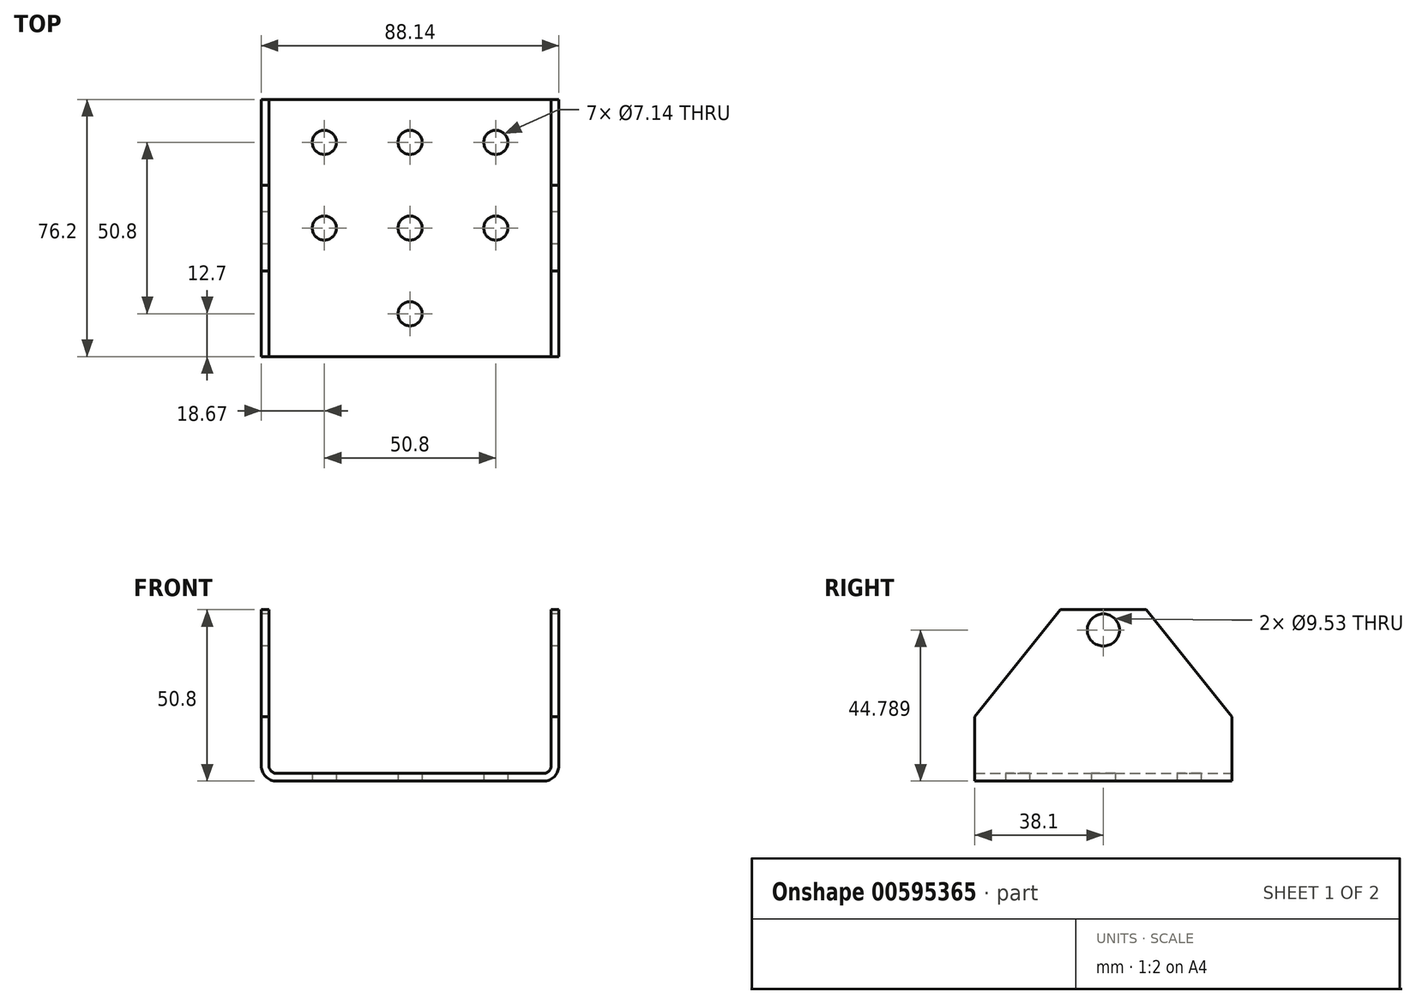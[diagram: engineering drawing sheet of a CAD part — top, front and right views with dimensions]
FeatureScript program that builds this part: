
annotation { "Feature Type Name" : "Feature", "Feature Type Description" : "" }
export const myFeature = defineFeature(function(context is Context, id is Id, definition is map)
    precondition{}
    {
        {
            var Q0;
            Q0=qCreatedBy(makeId("Front.planeOp"),FACE);
            var sketch = newSketch(context, id + "F0", { "sketchPlane" : qUnion([Q0])});
            skLineSegment(sketch, "E0", {"start": v(44.07, 50.8) * mm, "end": v(44.07, 4.57) * mm});
            skLineSegment(sketch, "E1", {"start": v(39.5, 0) * mm, "end": v(-39.5, 0) * mm});
            skLineSegment(sketch, "E2", {"start": v(-44.07, 4.57) * mm, "end": v(-44.07, 50.8) * mm});
            skLineSegment(sketch, "E3.0", {"start": v(-41.78, 4.57) * mm, "end": v(-41.78, 50.8) * mm});
            skLineSegment(sketch, "E3.1", {"start": v(39.5, 2.29) * mm, "end": v(-39.5, 2.29) * mm});
            skLineSegment(sketch, "E3.2", {"start": v(41.78, 50.8) * mm, "end": v(41.78, 4.57) * mm});
            skLineSegment(sketch, "E4", {"start": v(41.78, 50.8) * mm, "end": v(44.07, 50.8) * mm});
            skLineSegment(sketch, "E5", {"start": v(-41.78, 50.8) * mm, "end": v(-44.07, 50.8) * mm});
            skLineSegment(sketch, "E6", {"start": v(60.83, -227.83) * mm, "end": v(60.83, -317.3) * mm, "construction": true});
            skPoint(sketch, "E7.visualSharp", {"position": v(41.78, 2.29) * mm});
            skArc(sketch, "E7.filletArc", {"start": v(39.5, 2.29) * mm, "mid": v(41.11, 2.96) * mm, "end": v(41.78, 4.57) * mm});
            skPoint(sketch, "E8.visualSharp", {"position": v(-41.78, 2.29) * mm});
            skArc(sketch, "E8.filletArc", {"start": v(-41.78, 4.57) * mm, "mid": v(-41.11, 2.96) * mm, "end": v(-39.5, 2.29) * mm});
            skPoint(sketch, "E9.visualSharp", {"position": v(44.07, 0) * mm});
            skArc(sketch, "E9.filletArc", {"start": v(39.5, 0) * mm, "mid": v(42.73, 1.34) * mm, "end": v(44.07, 4.57) * mm});
            skPoint(sketch, "E10.visualSharp", {"position": v(-44.07, 0) * mm});
            skArc(sketch, "E10.filletArc", {"start": v(-44.07, 4.57) * mm, "mid": v(-42.73, 1.34) * mm, "end": v(-39.5, 0) * mm});
            skPoint(sketch, "E11", {"position": v(0, 0) * mm});
            skSolve(sketch);
        }
        {
            var Q0;
            Q0=makeQuery(id+"F0.imprint","IMPRINT",FACE,{"disambiguationData":[TD([[makeQuery(id+"F0.imprint","IMPRINT",EDGE,{"derivedFrom":sQuery(id+"F0.wireOp",EDGE,"E0")}),-1.0]])]});
            extrude(context, id + "F1", {"entities" : qUnion([Q0]), "endBound" : BoundingType.SYMMETRIC, "depth" : 76.2 * mm, "offsetDistance" : 25.4 * mm});
        }
        {
            var Q0;
            Q0=makeQuery(id+"F1.opExtrude","SWEPT_FACE",FACE,{"disambiguationData":[OSD([sQuery(id+"F0.wireOp",EDGE,"E2")])]});
            var sketch = newSketch(context, id + "F2", { "sketchPlane" : qUnion([Q0])});
            skLineSegment(sketch, "E12", {"start": v(38.1, 19.05) * mm, "end": v(12.7, 50.8) * mm});
            skLineSegment(sketch, "E13", {"start": v(12.7, 50.8) * mm, "end": v(38.1, 50.8) * mm});
            skLineSegment(sketch, "E14", {"start": v(38.1, 50.8) * mm, "end": v(38.1, 19.05) * mm});
            skLineSegment(sketch, "E15", {"start": v(0, -13.14) * mm, "end": v(0, -88.45) * mm, "construction": true});
            skLineSegment(sketch, "E16.MirrorCS", {"start": v(-38.1, 50.8) * mm, "end": v(-38.1, 19.05) * mm});
            skLineSegment(sketch, "E17.MirrorCS", {"start": v(-38.1, 19.05) * mm, "end": v(-12.7, 50.8) * mm});
            skLineSegment(sketch, "E18.MirrorCS", {"start": v(-12.7, 50.8) * mm, "end": v(-38.1, 50.8) * mm});
            skCircle(sketch, "E19", {"center": v(0, 44.79) * mm, "radius": 4.76 * mm});
            skPoint(sketch, "E20", {"position": v(0, 4.57) * mm});
            skSolve(sketch);
        }
        {
            var Q0;
            Q0=makeQuery(id+"F2.imprint","IMPRINT",FACE,{"disambiguationData":[TD([[makeQuery(id+"F2.imprint","IMPRINT",EDGE,{"derivedFrom":sQuery(id+"F2.wireOp",EDGE,"E12")}),-1.0]])]});
            var Q1;
            Q1=makeQuery(id+"F2.imprint","IMPRINT",FACE,{"disambiguationData":[TD([[makeQuery(id+"F2.imprint","IMPRINT",EDGE,{"derivedFrom":sQuery(id+"F2.wireOp",EDGE,"E19")}),1.0]])]});
            var Q2;
            Q2=makeQuery(id+"F2.imprint","IMPRINT",FACE,{"disambiguationData":[TD([[makeQuery(id+"F2.imprint","IMPRINT",EDGE,{"derivedFrom":sQuery(id+"F2.wireOp",EDGE,"E16.MirrorCS")}),-1.0]])]});
            extrude(context, id + "F3", {"entities" : qUnion([Q0, Q1, Q2]), "operationType" : NewBodyOperationType.REMOVE, "endBound" : BoundingType.THROUGH_ALL, "oppositeDirection" : true, "depth" : 25.4 * mm, "offsetDistance" : 25.4 * mm});
        }
        {
            var Q0;
            Q0=makeQuery(id+"F1.opExtrude","SWEPT_FACE",FACE,{"disambiguationData":[OSD([sQuery(id+"F0.wireOp",EDGE,"E1")])]});
            var sketch = newSketch(context, id + "F4", { "sketchPlane" : qUnion([Q0])});
            skPoint(sketch, "E21", {"position": v(0, 0) * mm});
            skPoint(sketch, "E22", {"position": v(-25.4, 0) * mm});
            skPoint(sketch, "E23", {"position": v(25.4, 0) * mm});
            skPoint(sketch, "E24", {"position": v(25.4, -25.4) * mm});
            skPoint(sketch, "E25", {"position": v(0, -25.4) * mm});
            skPoint(sketch, "E26", {"position": v(-25.4, -25.4) * mm});
            skPoint(sketch, "E27", {"position": v(0, 25.4) * mm});
            skSolve(sketch);
        }
        {
            var Q0;
            Q0=sQuery(id+"F4.wireOp",VERTEX,"E27");
            var Q1;
            Q1=sQuery(id+"F4.wireOp",VERTEX,"E23");
            var Q2;
            Q2=sQuery(id+"F4.wireOp",VERTEX,"E21");
            var Q3;
            Q3=sQuery(id+"F4.wireOp",VERTEX,"E22");
            var Q4;
            Q4=sQuery(id+"F4.wireOp",VERTEX,"E26");
            var Q5;
            Q5=sQuery(id+"F4.wireOp",VERTEX,"E25");
            var Q6;
            Q6=sQuery(id+"F4.wireOp",VERTEX,"E24");
            var Q7;
            Q7=makeQuery(id+"F1.opExtrude","SWEPT_BODY",BODY,{"disambiguationData":[OSD([sQuery(id+"F0.wireOp",EDGE,"E0"),sQuery(id+"F0.wireOp",EDGE,"E1"),sQuery(id+"F0.wireOp",EDGE,"E2"),sQuery(id+"F0.wireOp",EDGE,"E3.0"),sQuery(id+"F0.wireOp",EDGE,"E3.1"),sQuery(id+"F0.wireOp",EDGE,"E3.2"),sQuery(id+"F0.wireOp",EDGE,"E4"),sQuery(id+"F0.wireOp",EDGE,"E5"),sQuery(id+"F0.wireOp",EDGE,"E7.filletArc"),sQuery(id+"F0.wireOp",EDGE,"E8.filletArc"),sQuery(id+"F0.wireOp",EDGE,"E9.filletArc"),sQuery(id+"F0.wireOp",EDGE,"E10.filletArc")])]});
            hole(context, id + "F5", {"style" : HoleStyle.SIMPLE, "endStyle" : HoleEndStyle.THROUGH, "holeDiameter" : 7.14 * mm, "majorDiameter" : 6.35 * mm, "tappedDepth" : 12.7 * mm, "tapClearance" : 3, "locations" : qUnion([Q0, Q1, Q2, Q3, Q4, Q5, Q6]), "scope" : qUnion([Q7])});
        }
    });
